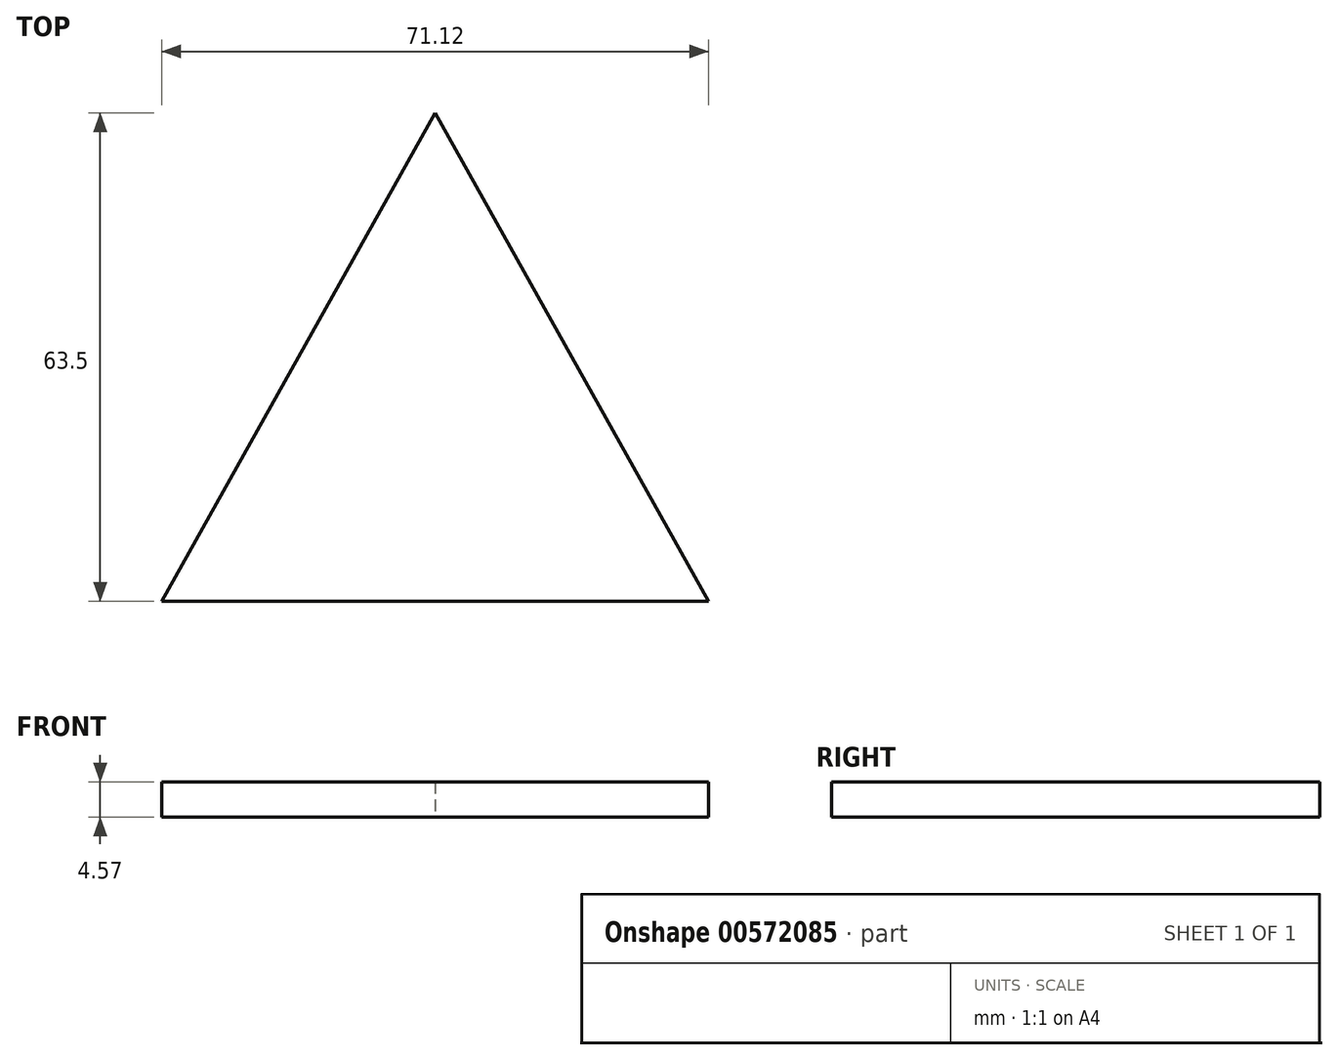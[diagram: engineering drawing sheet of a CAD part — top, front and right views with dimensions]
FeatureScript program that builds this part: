
annotation { "Feature Type Name" : "Feature", "Feature Type Description" : "" }
export const myFeature = defineFeature(function(context is Context, id is Id, definition is map)
    precondition{}
    {
        {
            var Q0;
            Q0=qCreatedBy(makeId("Top.planeOp"),FACE);
            var sketch = newSketch(context, id + "F0", { "sketchPlane" : qUnion([Q0])});
            skLineSegment(sketch, "E0.bottom", {"start": v(-25.35, 21.05) * mm, "end": v(45.77, 21.05) * mm});
            skLineSegment(sketch, "E0.top", {"start": v(-25.35, -42.45) * mm, "end": v(45.77, -42.45) * mm});
            skLineSegment(sketch, "E0.left", {"start": v(-25.35, 21.05) * mm, "end": v(-25.35, -42.45) * mm});
            skLineSegment(sketch, "E0.right", {"start": v(45.77, 21.05) * mm, "end": v(45.77, -42.45) * mm});
            skLineSegment(sketch, "E1", {"start": v(10.21, 21.05) * mm, "end": v(-25.35, -42.45) * mm});
            skLineSegment(sketch, "E2", {"start": v(10.21, 21.05) * mm, "end": v(45.77, -42.45) * mm});
            skSolve(sketch);
        }
        {
            var Q0;
            Q0=makeQuery(id+"F0.imprint","IMPRINT",FACE,{"disambiguationData":[TD([[makeQuery(id+"F0.imprint","IMPRINT",EDGE,{"derivedFrom":sQuery(id+"F0.wireOp",EDGE,"E1")}),1.0]])]});
            extrude(context, id + "F1", {"entities" : qUnion([Q0]), "depth" : 4.57 * mm, "offsetDistance" : 25.4 * mm});
        }
    });
